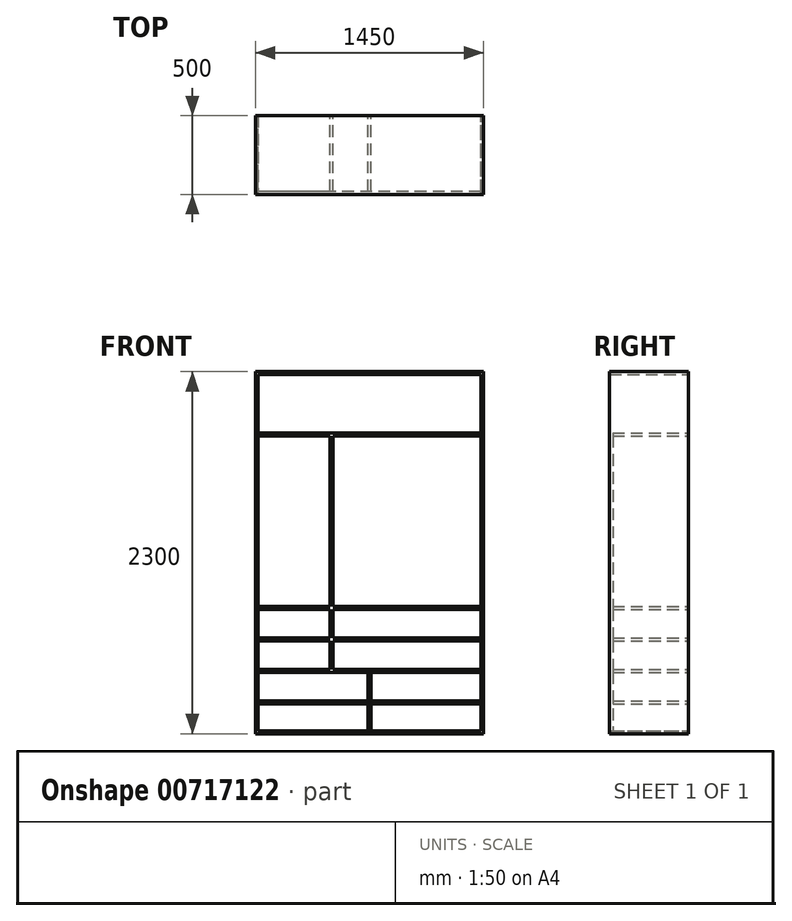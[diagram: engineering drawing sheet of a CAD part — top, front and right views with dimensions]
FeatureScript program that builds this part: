
annotation { "Feature Type Name" : "Feature", "Feature Type Description" : "" }
export const myFeature = defineFeature(function(context is Context, id is Id, definition is map)
    precondition{}
    {
        {
            var Q0;
            Q0=qCreatedBy(makeId("Front.planeOp"),FACE);
            var sketch = newSketch(context, id + "F0", { "sketchPlane" : qUnion([Q0])});
            skLineSegment(sketch, "E0.bottom", {"start": v(725, -1150) * mm, "end": v(-725, -1150) * mm});
            skLineSegment(sketch, "E0.top", {"start": v(725, 1150) * mm, "end": v(-725, 1150) * mm});
            skLineSegment(sketch, "E0.left", {"start": v(725, -1150) * mm, "end": v(725, 1150) * mm});
            skLineSegment(sketch, "E0.right", {"start": v(-725, -1150) * mm, "end": v(-725, 1150) * mm});
            skPoint(sketch, "E0.middle", {"position": v(0, 0) * mm});
            skSolve(sketch);
        }
        {
            var Q0;
            Q0=qSketchRegion(id+"F0",true);
            extrude(context, id + "F1", {"entities" : qUnion([Q0]), "depth" : 500 * mm, "offsetDistance" : 25 * mm});
        }
        {
            var Q0;
            Q0=makeQuery(id+"F0.imprint","IMPRINT",FACE,{"disambiguationData":[TD([[makeQuery(id+"F0.imprint","IMPRINT",EDGE,{"derivedFrom":sQuery(id+"F0.wireOp",EDGE,"E0.bottom")}),-1.0]])]});
            var sketch = newSketch(context, id + "F2", { "sketchPlane" : qUnion([Q0])});
            skLineSegment(sketch, "E1.0", {"start": v(707, 1132) * mm, "end": v(-707, 1132) * mm});
            skLineSegment(sketch, "E1.1", {"start": v(707, 1132) * mm, "end": v(707, -1132) * mm});
            skLineSegment(sketch, "E1.2", {"start": v(707, -1132) * mm, "end": v(-707, -1132) * mm});
            skLineSegment(sketch, "E1.3", {"start": v(-707, -1132) * mm, "end": v(-707, 1132) * mm});
            skSolve(sketch);
        }
        {
            var Q0;
            Q0=qSketchRegion(id+"F2",true);
            extrude(context, id + "F3", {"entities" : qUnion([Q0]), "operationType" : NewBodyOperationType.REMOVE, "depth" : 500 * mm, "offsetDistance" : 25 * mm});
        }
        {
            var Q0;
            Q0=makeQuery(id+"F0.imprint","IMPRINT",FACE,{"disambiguationData":[TD([[makeQuery(id+"F0.imprint","IMPRINT",EDGE,{"derivedFrom":sQuery(id+"F0.wireOp",EDGE,"E0.bottom")}),-1.0]])]});
            var sketch = newSketch(context, id + "F4", { "sketchPlane" : qUnion([Q0])});
            skLineSegment(sketch, "E2.0.left", {"start": v(725, -960) * mm, "end": v(-725, -960) * mm});
            skLineSegment(sketch, "E2.0.right", {"start": v(725, -942) * mm, "end": v(-233, -942) * mm});
            skLineSegment(sketch, "E2.1.left", {"start": v(725, -760) * mm, "end": v(-233, -760) * mm});
            skLineSegment(sketch, "E2.1.right", {"start": v(725, -742) * mm, "end": v(-233, -742) * mm});
            skLineSegment(sketch, "E2.2.left", {"start": v(-233, 742) * mm, "end": v(-233, -342) * mm});
            skLineSegment(sketch, "E2.2.right", {"start": v(-251, 742) * mm, "end": v(-251, -342) * mm});
            skLineSegment(sketch, "E2.3.left", {"start": v(725, 742) * mm, "end": v(-233, 742) * mm});
            skLineSegment(sketch, "E2.3.right", {"start": v(725, 760) * mm, "end": v(-725, 760) * mm});
            skLineSegment(sketch, "E2.4.left", {"start": v(725, -360) * mm, "end": v(-233, -360) * mm});
            skLineSegment(sketch, "E2.4.right", {"start": v(725, -342) * mm, "end": v(-233, -342) * mm});
            skLineSegment(sketch, "E2.5.left", {"start": v(725, -560) * mm, "end": v(-233, -560) * mm});
            skLineSegment(sketch, "E2.5.right", {"start": v(725, -542) * mm, "end": v(-233, -542) * mm});
            skLineSegment(sketch, "E3.0", {"start": v(725, 760) * mm, "end": v(725, 742) * mm});
            skLineSegment(sketch, "E4.trimOffspring", {"start": v(-251, 742) * mm, "end": v(-725, 742) * mm});
            skLineSegment(sketch, "E5.0", {"start": v(-725, -960) * mm, "end": v(-725, -942) * mm});
            skLineSegment(sketch, "E6.trimOffspring", {"start": v(-725, 742) * mm, "end": v(-725, 760) * mm});
            skLineSegment(sketch, "E7.trimOffspring", {"start": v(-725, -360) * mm, "end": v(-725, -342) * mm});
            skLineSegment(sketch, "E8.trimOffspring", {"start": v(-251, -342) * mm, "end": v(-725, -342) * mm});
            skLineSegment(sketch, "E9.trimOffspring", {"start": v(-251, -360) * mm, "end": v(-251, -542) * mm});
            skLineSegment(sketch, "E10.trimOffspring", {"start": v(-251, -360) * mm, "end": v(-725, -360) * mm});
            skLineSegment(sketch, "E11.trimOffspring", {"start": v(-233, -360) * mm, "end": v(-233, -542) * mm});
            skLineSegment(sketch, "E12.trimOffspring", {"start": v(-251, -560) * mm, "end": v(-251, -742) * mm});
            skLineSegment(sketch, "E13.trimOffspring", {"start": v(-251, -542) * mm, "end": v(-725, -542) * mm});
            skLineSegment(sketch, "E14.trimOffspring", {"start": v(-251, -560) * mm, "end": v(-725, -560) * mm});
            skLineSegment(sketch, "E15.trimOffspring", {"start": v(-233, -560) * mm, "end": v(-233, -742) * mm});
            skLineSegment(sketch, "E16.trimOffspring", {"start": v(-251, -742) * mm, "end": v(-725, -742) * mm});
            skLineSegment(sketch, "E17.trimOffspring", {"start": v(-251, -760) * mm, "end": v(-725, -760) * mm});
            skLineSegment(sketch, "E18.trimOffspring", {"start": v(-725, -560) * mm, "end": v(-725, -542) * mm});
            skLineSegment(sketch, "E19.trimOffspring", {"start": v(-725, -760) * mm, "end": v(-725, -742) * mm});
            skLineSegment(sketch, "E20.trimOffspring", {"start": v(-251, -942) * mm, "end": v(-725, -942) * mm});
            skLineSegment(sketch, "E21.trimOffspring", {"start": v(725, -342) * mm, "end": v(725, -360) * mm});
            skLineSegment(sketch, "E22.trimOffspring", {"start": v(725, -542) * mm, "end": v(725, -560) * mm});
            skLineSegment(sketch, "E23.trimOffspring", {"start": v(725, -742) * mm, "end": v(725, -760) * mm});
            skLineSegment(sketch, "E24.trimOffspring", {"start": v(725, -942) * mm, "end": v(725, -960) * mm});
            skLineSegment(sketch, "E25", {"start": v(-233, -760) * mm, "end": v(-251, -760) * mm});
            skLineSegment(sketch, "E26", {"start": v(-233, -942) * mm, "end": v(-251, -942) * mm});
            skSolve(sketch);
        }
        {
            var Q0;
            Q0=qSketchRegion(id+"F4",true);
            extrude(context, id + "F5", {"entities" : qUnion([Q0]), "operationType" : NewBodyOperationType.ADD, "depth" : 480 * mm, "offsetDistance" : 25 * mm});
        }
        {
            var Q0;
            Q0=makeQuery(id+"F0.imprint","IMPRINT",FACE,{"disambiguationData":[TD([[makeQuery(id+"F0.imprint","IMPRINT",EDGE,{"derivedFrom":sQuery(id+"F0.wireOp",EDGE,"E0.bottom")}),-1.0]])]});
            var sketch = newSketch(context, id + "F6", { "sketchPlane" : qUnion([Q0])});
            skLineSegment(sketch, "E27.0.left", {"start": v(9, -760) * mm, "end": v(9, -1132) * mm});
            skLineSegment(sketch, "E27.0.right", {"start": v(-9, -760) * mm, "end": v(-9, -1132) * mm});
            skLineSegment(sketch, "E28.0", {"start": v(9, -760) * mm, "end": v(-9, -760) * mm});
            skLineSegment(sketch, "E29.0", {"start": v(9, -1132) * mm, "end": v(-9, -1132) * mm});
            skPoint(sketch, "E30.orphan", {"position": v(707, -760) * mm});
            skPoint(sketch, "E31.orphan", {"position": v(-707, -760) * mm});
            skPoint(sketch, "E32.orphan", {"position": v(-707, -1132) * mm});
            skPoint(sketch, "E33.orphan", {"position": v(707, -1132) * mm});
            skSolve(sketch);
        }
        {
            var Q0;
            Q0=qSketchRegion(id+"F6",true);
            extrude(context, id + "F7", {"entities" : qUnion([Q0]), "depth" : 480 * mm, "offsetDistance" : 25 * mm});
        }
    });
